# Revit family: Lighting_Ceiling-Mounted_Nordlux_Mimi-2-spot-Ceiling
name_source: partatom
category: Lighting Fixtures
revit_build: Autodesk Revit 2018 (Build: 20190510_1515(x64)
units: mm (PartAtom-declared; Revit-internal decimal feet)

## family parameters
Cut with Voids When Loaded = No
Host = Face
Light Source = No
OmniClass Number = 23.35.47.11
OmniClass Title = Lighting Fixtures
Part Type = Normal
Room Calculation Point = No
Round Connector Dimension = Use Diameter
Shared = No

## types (2) — shared parameters
Apparent Load = 12 VA
BIMobject category = Ceiling Mounted
Beam angle = 44.00°
CQS = 80.9
CRI / Ra = 81.2
Default Elevation = 1219 mm
Description = The slim and elegant design of the Mimi spots by Bønnelycke MDD fits perfectly in a hallway, kitchen or any other space that needs a pleasant, directional light. The spots can be turned and tilted to light up specific areas or larger surfaces. Soft golden details add a unique touch to the classic design.
Design country = Denmark
Edition number = 1
Flicker frequency = 100 Hz
IFC Classification = Light Fixture
Installation instructions = https://asset.productmarketingcloud.com
Lens material = Nordlux - Glass - Milky glass
Manufacturer = Nordlux
Manufacturer country = China
Manufacturer name = Nordlux
Material main = Metal
Material secondary = Plastic
Model = Mimi 2-spot Ceiling
NominalVoltage = 230 V
OmniClass Code = 23-35 47 11
OmniClass Description = Lighting Fixtures
Peak [cd] = 1364
Power factor = 0.91
Product Guid = 23f446de-aec8-421f-9e50-6df4afbe8d67
Product SKU = Mimi2-spot-Ceiling
Product data url = https://bimobject.com
Product family = Lighting
Product group = Ceiling
Product name = Mimi 2-spot Ceiling
Product url = https://nordlux.com
QR code = https://bimobject.com
Shade material = Nordlux - Metal - Brass
TM30 Rf = 84.3
TM30 Rg = 94.7
URL = www.nordlux.com
Weight Net (Kg) = 0,93
Youtube clip = https://www.youtube.com

## per-type parameters (varying)
| type | Body material | EANNumber |
| ART - (2120456001) Finish colour - (White) | Nordlux  - Metal  - White | 2120456001 |
| ART - (2120456003) Finish colour - (Black) | Nordlux  - Metal  - Black | 2120456003 |

## geometry (parser evidence)
native form markers: Sweep x7
no freeform markers — native parametric forms only
